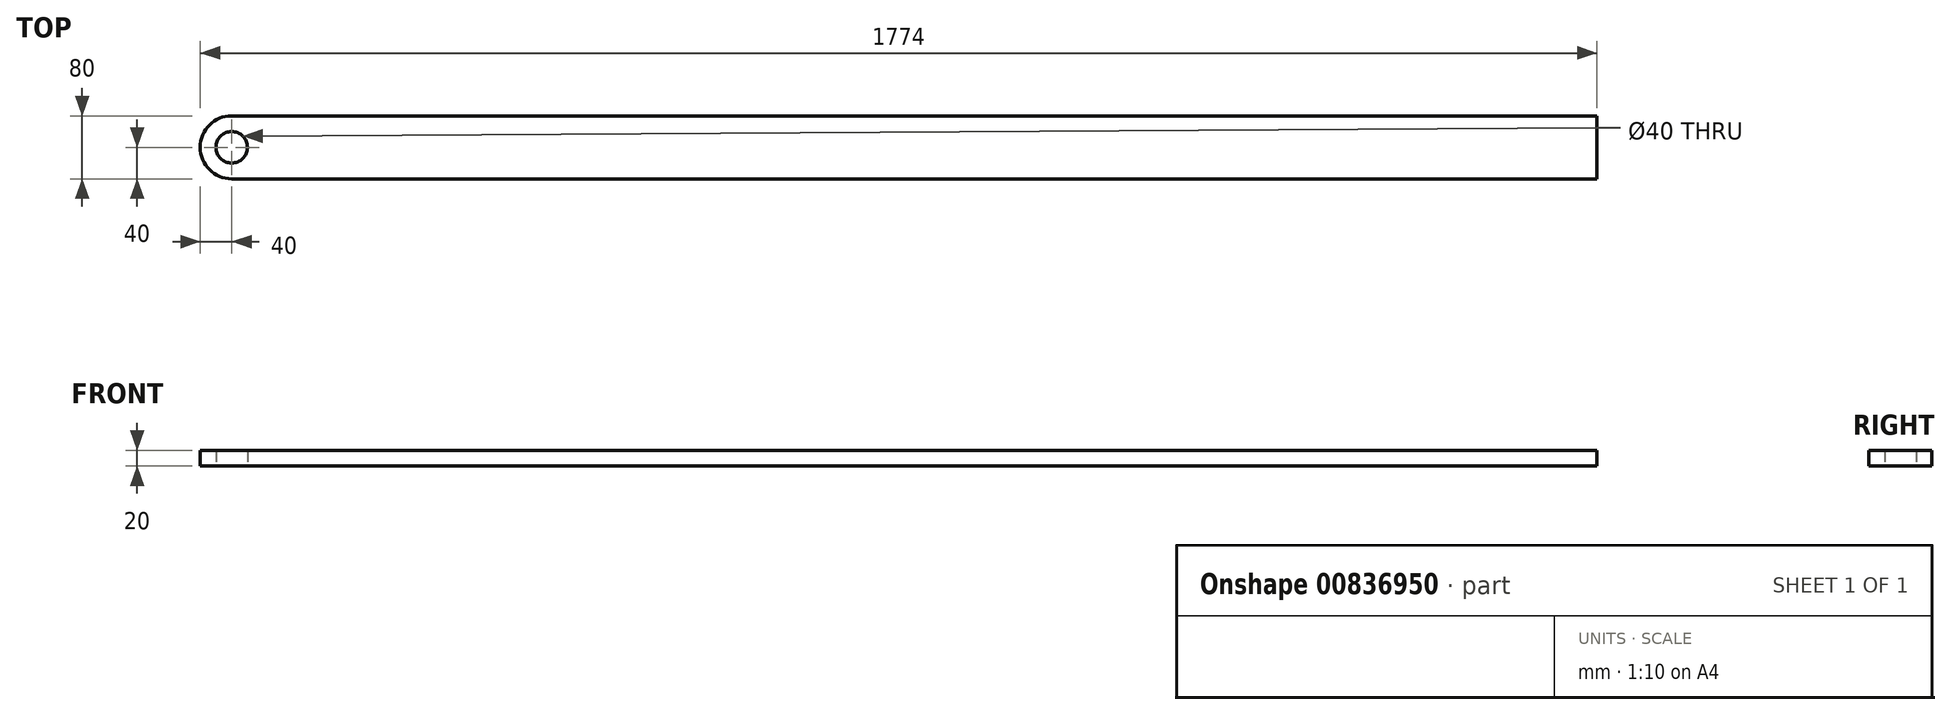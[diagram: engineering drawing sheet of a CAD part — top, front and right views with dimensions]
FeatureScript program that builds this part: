
annotation { "Feature Type Name" : "Feature", "Feature Type Description" : "" }
export const myFeature = defineFeature(function(context is Context, id is Id, definition is map)
    precondition{}
    {
        {
            var Q0;
            Q0=qCreatedBy(makeId("Top.planeOp"),FACE);
            var sketch = newSketch(context, id + "F0", { "sketchPlane" : qUnion([Q0])});
            skCircle(sketch, "E0", {"center": v(0, 0) * mm, "radius": 20 * mm});
            skLineSegment(sketch, "E1", {"start": v(0, 0) * mm, "end": v(3468, 0) * mm});
            skLineSegment(sketch, "E2", {"start": v(1734, 0) * mm, "end": v(1734, 414.02) * mm});
            skLineSegment(sketch, "E3", {"start": v(1734, 0) * mm, "end": v(1734, -40) * mm});
            skLineSegment(sketch, "E4", {"start": v(1734, -40) * mm, "end": v(0, -40) * mm});
            skLineSegment(sketch, "E5.MirrorCS", {"start": v(1734, 40) * mm, "end": v(0, 40) * mm});
            skArc(sketch, "E6", {"start": v(0, 40) * mm, "mid": v(-40, 0) * mm, "end": v(0, -40) * mm});
            skArc(sketch, "E7.MirrorCS", {"start": v(3468, 40) * mm, "mid": v(3508, 0) * mm, "end": v(3468, -40) * mm});
            skCircle(sketch, "E8.MirrorC", {"center": v(3468, 0) * mm, "radius": 20 * mm});
            skLineSegment(sketch, "E9.MirrorCS", {"start": v(1734, 40) * mm, "end": v(3468, 40) * mm});
            skLineSegment(sketch, "E10.MirrorCS", {"start": v(1734, -40) * mm, "end": v(3468, -40) * mm});
            skSolve(sketch);
        }
        {
            var Q0;
            Q0=makeQuery(id+"F0.imprint","IMPRINT",FACE,{"disambiguationData":[TD([[makeQuery(id+"F0.imprint","IMPRINT",EDGE,{"derivedFrom":sQuery(id+"F0.wireOp",EDGE,"E0")}),-1.0]])]});
            var Q1;
            Q1=makeQuery(id+"F0.imprint","IMPRINT",FACE,{"disambiguationData":[TD([[makeQuery(id+"F0.imprint","IMPRINT",EDGE,{"derivedFrom":sQuery(id+"F0.wireOp",EDGE,"E7.MirrorCS")}),-1.0]])]});
            extrude(context, id + "F1", {"entities" : qUnion([Q0, Q1]), "endBound" : BoundingType.SYMMETRIC, "depth" : 20 * mm, "offsetDistance" : 25 * mm});
        }
    });
